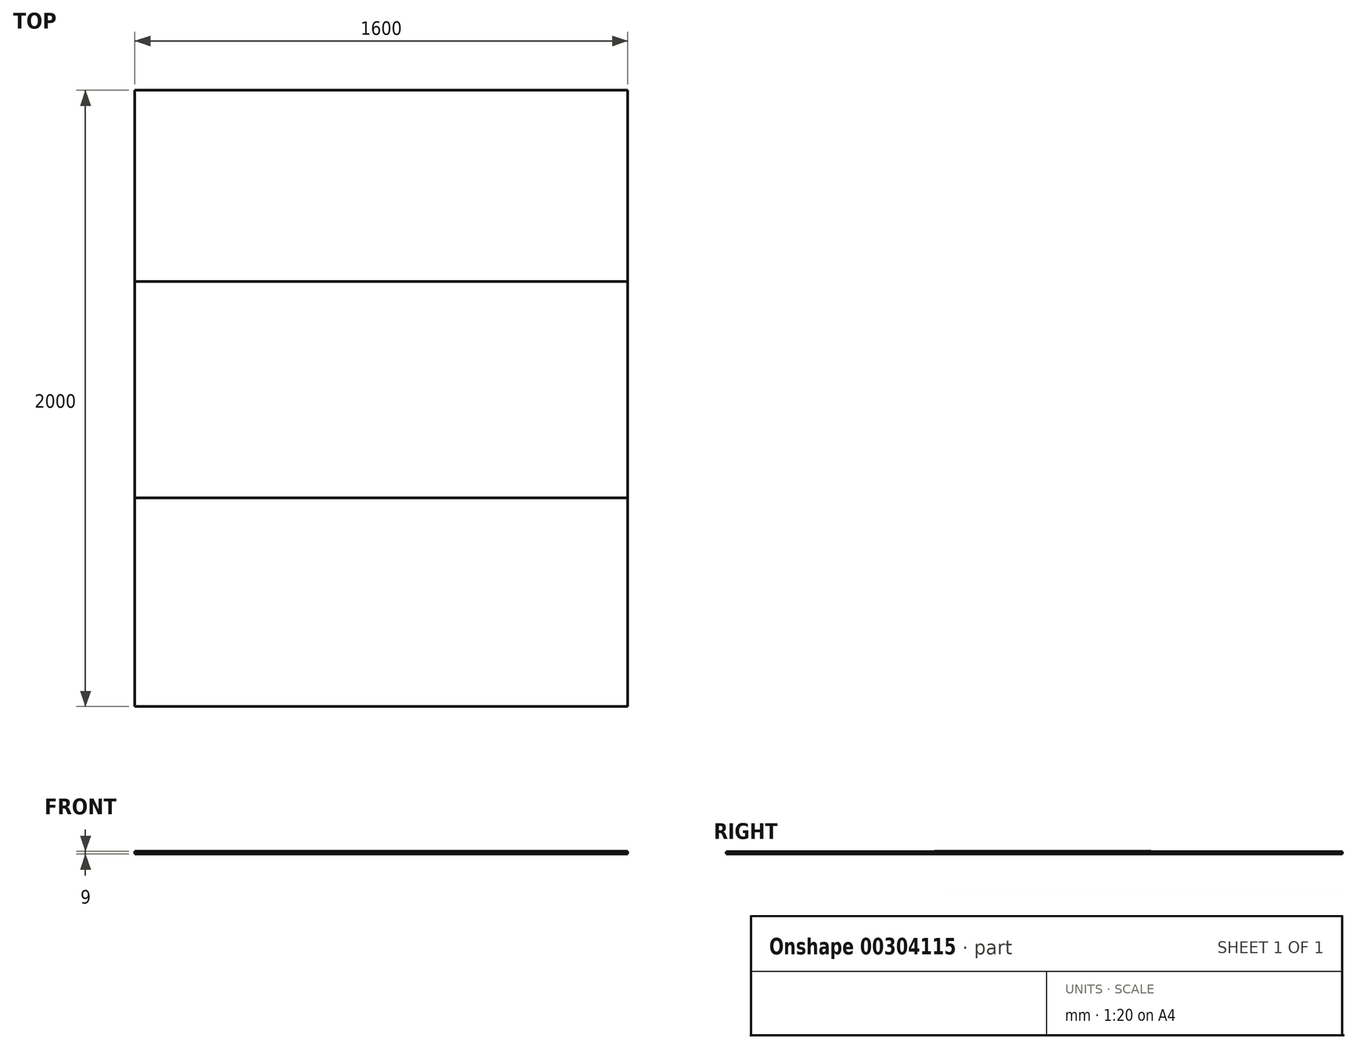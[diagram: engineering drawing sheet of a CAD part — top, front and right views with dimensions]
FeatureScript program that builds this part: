
annotation { "Feature Type Name" : "Feature", "Feature Type Description" : "" }
export const myFeature = defineFeature(function(context is Context, id is Id, definition is map)
    precondition{}
    {
        {
            var Q0;
            Q0=qCreatedBy(makeId("Top.planeOp"),FACE);
            var sketch = newSketch(context, id + "F0", { "sketchPlane" : qUnion([Q0])});
            skLineSegment(sketch, "E0.bottom", {"start": v(-750.1, 1493.52) * mm, "end": v(849.9, 1493.52) * mm});
            skLineSegment(sketch, "E0.top", {"start": v(-750.1, -506.48) * mm, "end": v(849.9, -506.48) * mm});
            skLineSegment(sketch, "E0.left", {"start": v(-750.1, 1493.52) * mm, "end": v(-750.1, -506.48) * mm});
            skLineSegment(sketch, "E0.right", {"start": v(849.9, 1493.52) * mm, "end": v(849.9, -506.48) * mm});
            skSolve(sketch);
        }
        {
            var Q0;
            Q0=makeQuery(id+"F0.imprint","IMPRINT",FACE,{"disambiguationData":[TD([[makeQuery(id+"F0.imprint","IMPRINT",EDGE,{"derivedFrom":sQuery(id+"F0.wireOp",EDGE,"E0.bottom")}),-1.0]])]});
            extrude(context, id + "F1", {"entities" : qUnion([Q0]), "depth" : 8 * mm, "offsetDistance" : 25 * mm});
        }
        {
            var Q0;
            Q0=makeQuery(id+"F1.opExtrude","CAP_FACE",FACE,{"disambiguationData":[OSD([sQuery(id+"F0.wireOp",EDGE,"E0.bottom"),sQuery(id+"F0.wireOp",EDGE,"E0.top"),sQuery(id+"F0.wireOp",EDGE,"E0.left"),sQuery(id+"F0.wireOp",EDGE,"E0.right")])],"isStart":false});
            var sketch = newSketch(context, id + "F2", { "sketchPlane" : qUnion([Q0])});
            skLineSegment(sketch, "E1.bottom", {"start": v(-750.1, 872.99) * mm, "end": v(849.9, 872.99) * mm});
            skLineSegment(sketch, "E1.top", {"start": v(-750.1, 170.59) * mm, "end": v(849.9, 170.59) * mm});
            skLineSegment(sketch, "E1.left", {"start": v(-750.1, 872.99) * mm, "end": v(-750.1, 170.59) * mm});
            skLineSegment(sketch, "E1.right", {"start": v(849.9, 872.99) * mm, "end": v(849.9, 170.59) * mm});
            skSolve(sketch);
        }
        {
            var Q0;
            Q0=makeQuery(id+"F2.imprint","IMPRINT",FACE,{"disambiguationData":[TD([[makeQuery(id+"F2.imprint","IMPRINT",EDGE,{"derivedFrom":sQuery(id+"F2.wireOp",EDGE,"E1.bottom")}),-1.0]])]});
            extrude(context, id + "F3", {"entities" : qUnion([Q0]), "depth" : 1 * mm, "offsetDistance" : 25 * mm});
        }
    });
